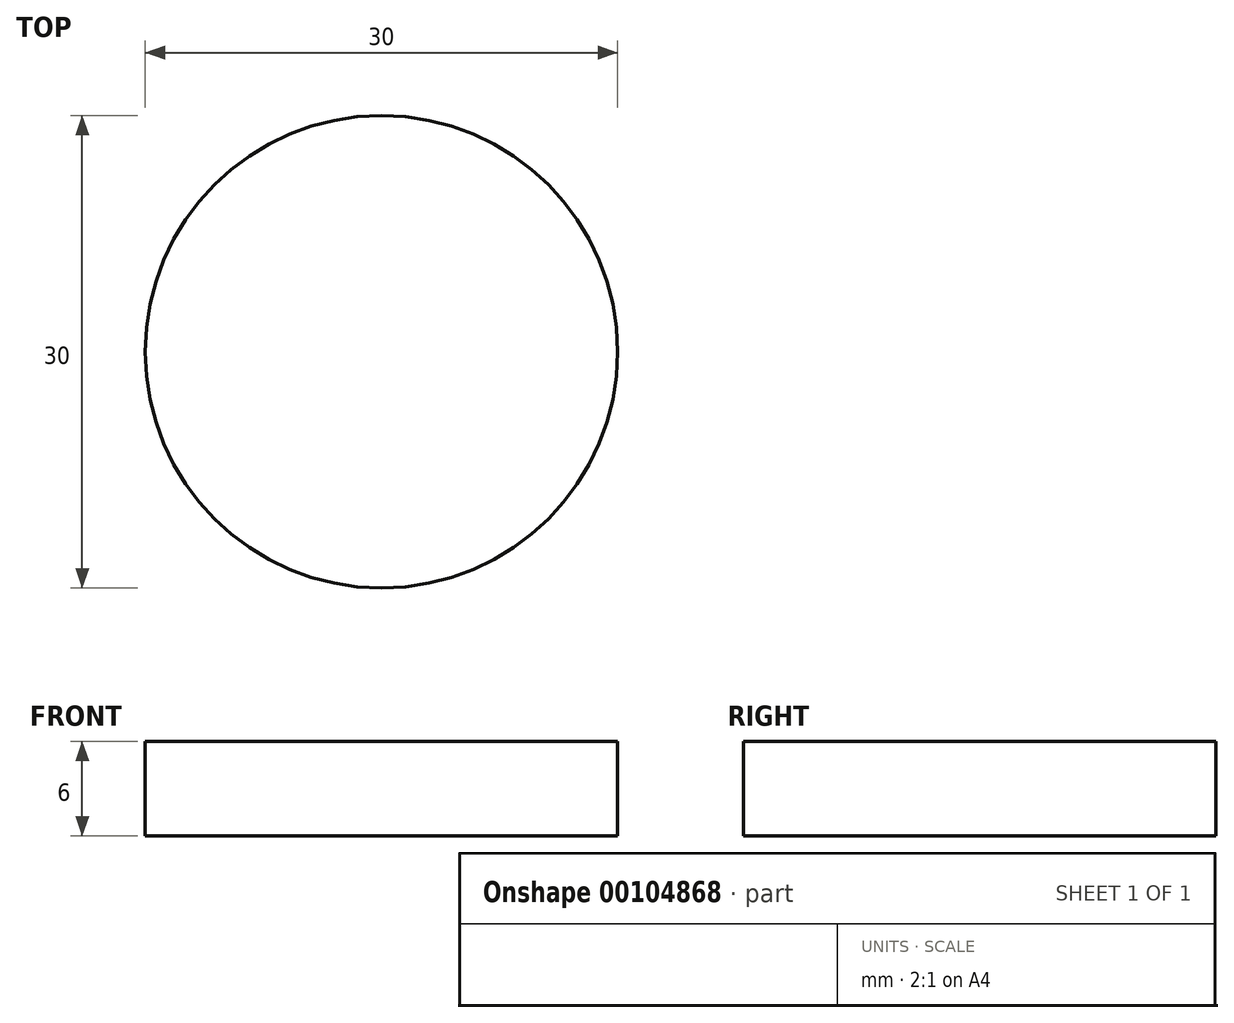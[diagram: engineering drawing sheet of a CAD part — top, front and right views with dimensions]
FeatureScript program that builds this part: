
annotation { "Feature Type Name" : "Feature", "Feature Type Description" : "" }
export const myFeature = defineFeature(function(context is Context, id is Id, definition is map)
    precondition{}
    {
        {
            var Q0;
            Q0=qCreatedBy(makeId("Top.planeOp"),FACE);
            var sketch = newSketch(context, id + "F0", { "sketchPlane" : qUnion([Q0])});
            skCircle(sketch, "E0", {"center": v(0, 0) * mm, "radius": 15 * mm});
            skSolve(sketch);
        }
        {
            var Q0;
            Q0=makeQuery(id+"F0.imprint","IMPRINT",FACE,{"disambiguationData":[TD([[makeQuery(id+"F0.imprint","IMPRINT",EDGE,{"derivedFrom":sQuery(id+"F0.wireOp",EDGE,"E0")}),1.0]])]});
            extrude(context, id + "F1", {"entities" : qUnion([Q0]), "depth" : 6 * mm});
        }
    });
